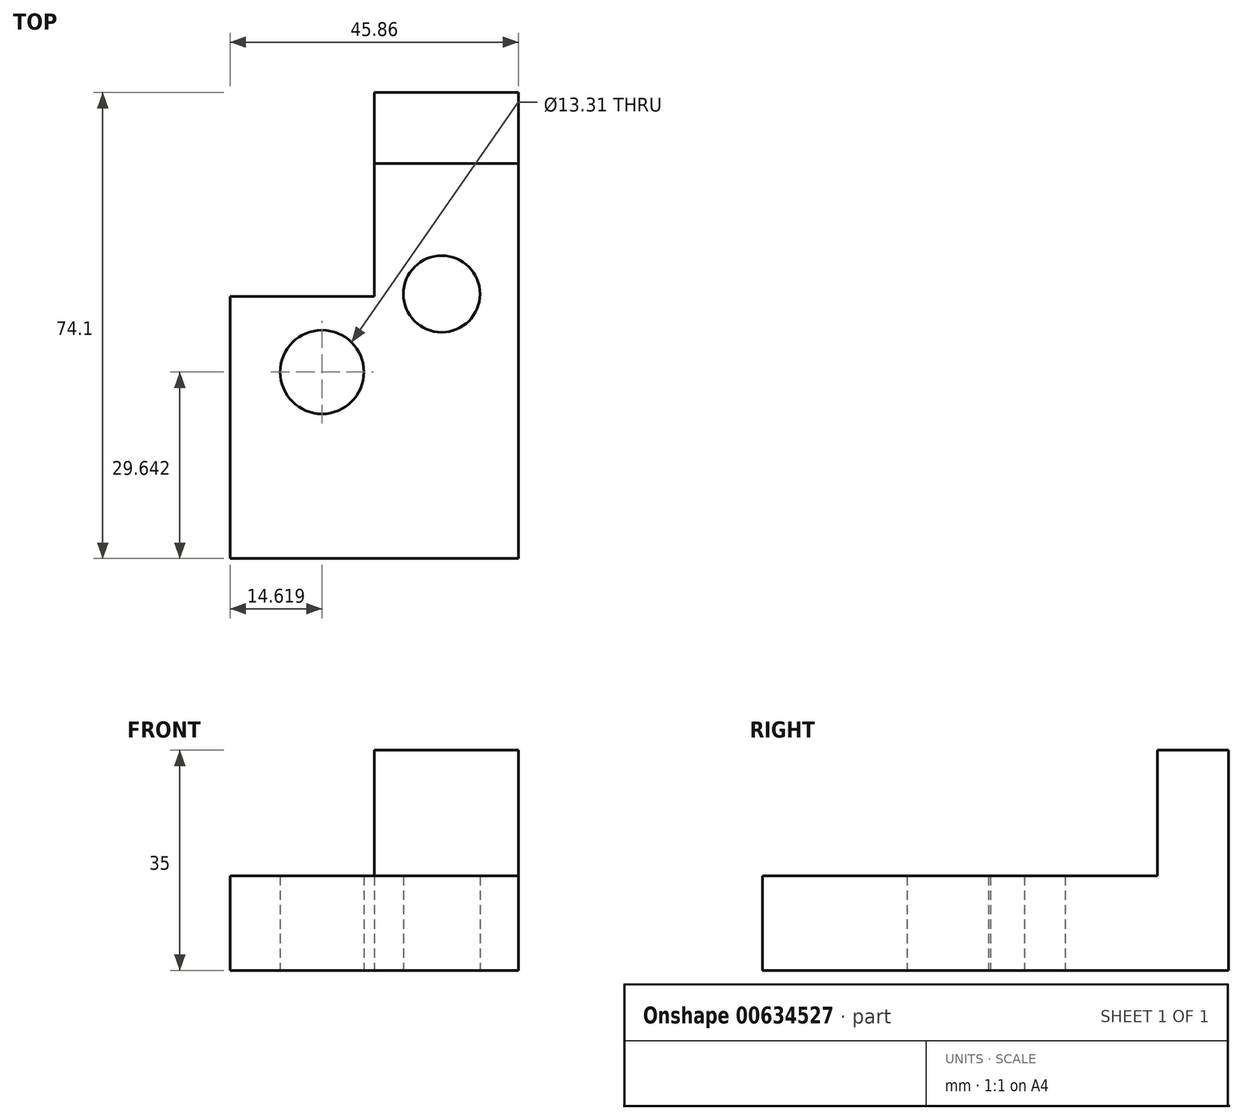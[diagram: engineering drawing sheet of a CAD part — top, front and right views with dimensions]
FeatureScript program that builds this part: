
annotation { "Feature Type Name" : "Feature", "Feature Type Description" : "" }
export const myFeature = defineFeature(function(context is Context, id is Id, definition is map)
    precondition{}
    {
        {
            var Q0;
            Q0=qCreatedBy(makeId("Top.planeOp"),FACE);
            var sketch = newSketch(context, id + "F0", { "sketchPlane" : qUnion([Q0])});
            skLineSegment(sketch, "E0.bottom", {"start": v(22.93, -20.83) * mm, "end": v(-22.93, -20.83) * mm});
            skLineSegment(sketch, "E0.top", {"start": v(0, 20.83) * mm, "end": v(-22.93, 20.83) * mm});
            skLineSegment(sketch, "E0.left", {"start": v(22.93, -20.83) * mm, "end": v(22.93, 20.83) * mm});
            skLineSegment(sketch, "E0.right", {"start": v(-22.93, -20.83) * mm, "end": v(-22.93, 20.83) * mm});
            skPoint(sketch, "E0.middle", {"position": v(0, 0) * mm});
            skLineSegment(sketch, "E1.bottom", {"start": v(-22.93, -20.83) * mm, "end": v(22.93, -20.83) * mm});
            skLineSegment(sketch, "E1.left", {"start": v(-22.93, -20.83) * mm, "end": v(-22.93, -10.41) * mm});
            skLineSegment(sketch, "E1.right", {"start": v(22.93, -20.83) * mm, "end": v(22.93, -10.41) * mm});
            skLineSegment(sketch, "E2.top", {"start": v(22.93, 53.27) * mm, "end": v(0, 53.27) * mm});
            skLineSegment(sketch, "E2.left", {"start": v(22.93, 20.83) * mm, "end": v(22.93, 53.27) * mm});
            skLineSegment(sketch, "E2.right", {"start": v(0, 20.83) * mm, "end": v(0, 53.27) * mm});
            skCircle(sketch, "E3", {"center": v(10.71, 21.23) * mm, "radius": 6.1 * mm});
            skCircle(sketch, "E4", {"center": v(-8.31, 8.81) * mm, "radius": 6.66 * mm});
            skSolve(sketch);
        }
        {
            var Q0;
            Q0 = qSketchRegion(id + "F0", true);
            extrude(context, id + "F1", {"entities" : qUnion([Q0]), "depth" : 15 * mm, "offsetDistance" : 25.4 * mm});
        }
        {
            var Q0;
            Q0=makeQuery(id+"F1.opExtrude","CAP_FACE",FACE,{"disambiguationData":[OSD([sQuery(id+"F0.wireOp",EDGE,"E0.top"),sQuery(id+"F0.wireOp",EDGE,"E0.left"),sQuery(id+"F0.wireOp",EDGE,"E0.right"),sQuery(id+"F0.wireOp",EDGE,"E1.bottom"),sQuery(id+"F0.wireOp",EDGE,"E1.left"),sQuery(id+"F0.wireOp",EDGE,"E1.right"),sQuery(id+"F0.wireOp",EDGE,"E2.top"),sQuery(id+"F0.wireOp",EDGE,"E2.left"),sQuery(id+"F0.wireOp",EDGE,"E2.right"),sQuery(id+"F0.wireOp",EDGE,"E3"),sQuery(id+"F0.wireOp",EDGE,"E4")])],"isStart":false});
            var sketch = newSketch(context, id + "F2", { "sketchPlane" : qUnion([Q0])});
            skLineSegment(sketch, "E5.bottom", {"start": v(0, 53.27) * mm, "end": v(22.93, 53.27) * mm});
            skLineSegment(sketch, "E5.top", {"start": v(0, 41.99) * mm, "end": v(22.93, 41.99) * mm});
            skLineSegment(sketch, "E5.left", {"start": v(0, 53.27) * mm, "end": v(0, 41.99) * mm});
            skLineSegment(sketch, "E5.right", {"start": v(22.93, 53.27) * mm, "end": v(22.93, 41.99) * mm});
            skLineSegment(sketch, "E6.bottom", {"start": v(-22.93, -20.83) * mm, "end": v(22.93, -20.83) * mm});
            skLineSegment(sketch, "E6.top", {"start": v(-22.93, -5.32) * mm, "end": v(22.93, -5.32) * mm});
            skLineSegment(sketch, "E6.left", {"start": v(-22.93, -20.83) * mm, "end": v(-22.93, -5.32) * mm});
            skLineSegment(sketch, "E6.right", {"start": v(22.93, -20.83) * mm, "end": v(22.93, -5.32) * mm});
            skSolve(sketch);
        }
        {
            var Q0;
            Q0=makeQuery(id+"F2.imprint","IMPRINT",FACE,{"disambiguationData":[TD([[makeQuery(id+"F2.imprint","IMPRINT",EDGE,{"derivedFrom":sQuery(id+"F2.wireOp",EDGE,"E5.bottom")}),1.0]])]});
            var Q1;
            Q1=makeQuery(id+"F2.imprint","IMPRINT",FACE,{"disambiguationData":[TD([[makeQuery(id+"F2.imprint","IMPRINT",EDGE,{"derivedFrom":sQuery(id+"F2.wireOp",EDGE,"E6.bottom")}),1.0]])]});
            extrude(context, id + "F3", {"entities" : qUnion([Q0, Q1]), "operationType" : NewBodyOperationType.ADD, "depth" : 20 * mm, "offsetDistance" : 25 * mm});
        }
    });
